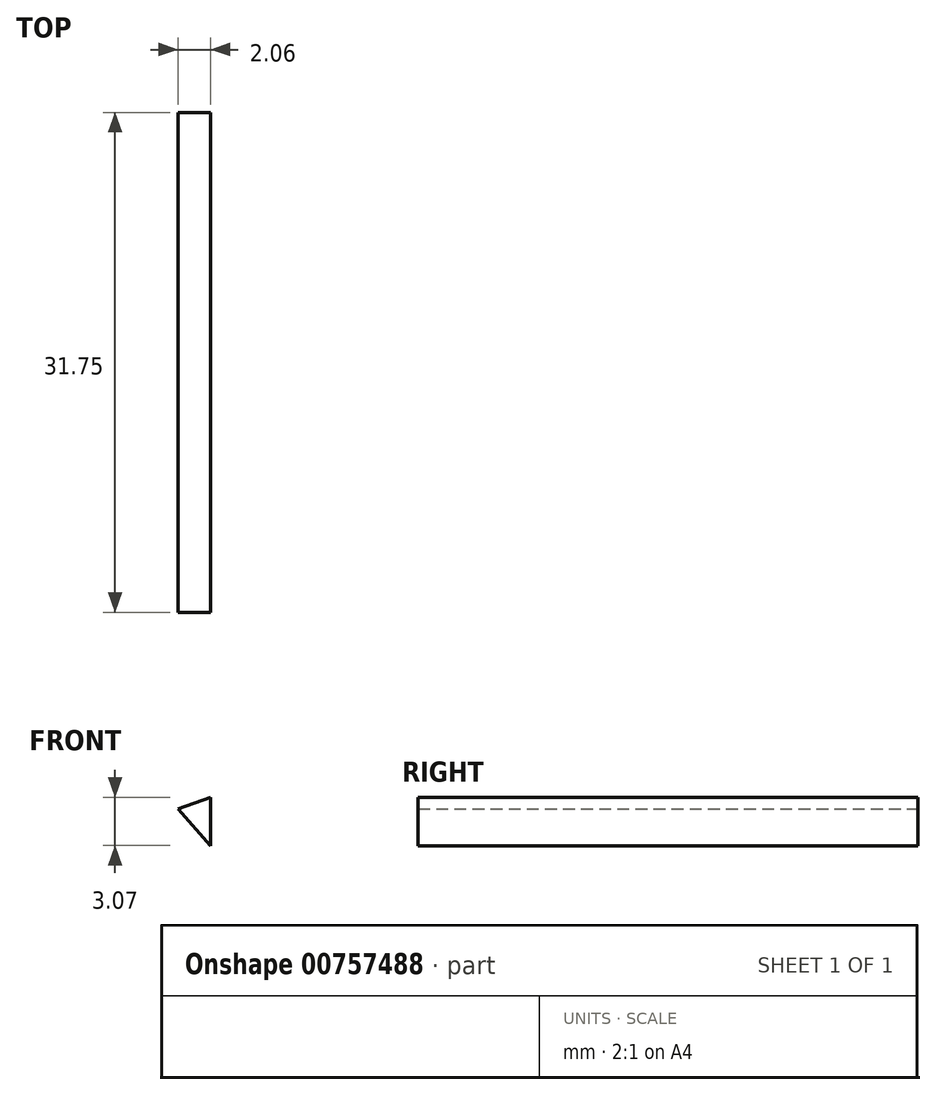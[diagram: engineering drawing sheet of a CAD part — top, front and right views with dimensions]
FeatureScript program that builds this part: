
annotation { "Feature Type Name" : "Feature", "Feature Type Description" : "" }
export const myFeature = defineFeature(function(context is Context, id is Id, definition is map)
    precondition{}
    {
        {
            var Q0;
            Q0=qCreatedBy(makeId("Front.planeOp"),FACE);
            var sketch = newSketch(context, id + "F0", { "sketchPlane" : qUnion([Q0])});
            skLineSegment(sketch, "E0", {"start": v(0, 30.86) * mm, "end": v(25.4, 30.86) * mm});
            skLineSegment(sketch, "E1", {"start": v(25.4, 30.86) * mm, "end": v(25.4, 0) * mm});
            skLineSegment(sketch, "E2", {"start": v(28.47, 8.3) * mm, "end": v(23.34, 14.1) * mm});
            skLineSegment(sketch, "E3", {"start": v(23.34, 14.1) * mm, "end": v(28.12, 15.81) * mm});
            skSolve(sketch);
        }
        {
            var Q0;
            Q0 = qSketchRegion(id + "F0", true);
            extrude(context, id + "F1", {"entities" : qUnion([Q0]), "surfaceOperationType" : NewSurfaceOperationType.ADD, "depth" : 31.75 * mm, "offsetDistance" : 25.4 * mm});
        }
        {
            var Q0;
            Q0=qCreatedBy(makeId("Front.planeOp"),FACE);
            cPlane(context, id + "F2", {"entities" : qUnion([Q0]), "cplaneType" : CPlaneType.OFFSET, "offset" : 25.4 * mm, "width" : 152.4 * mm, "height" : 152.4 * mm});
        }
    });
